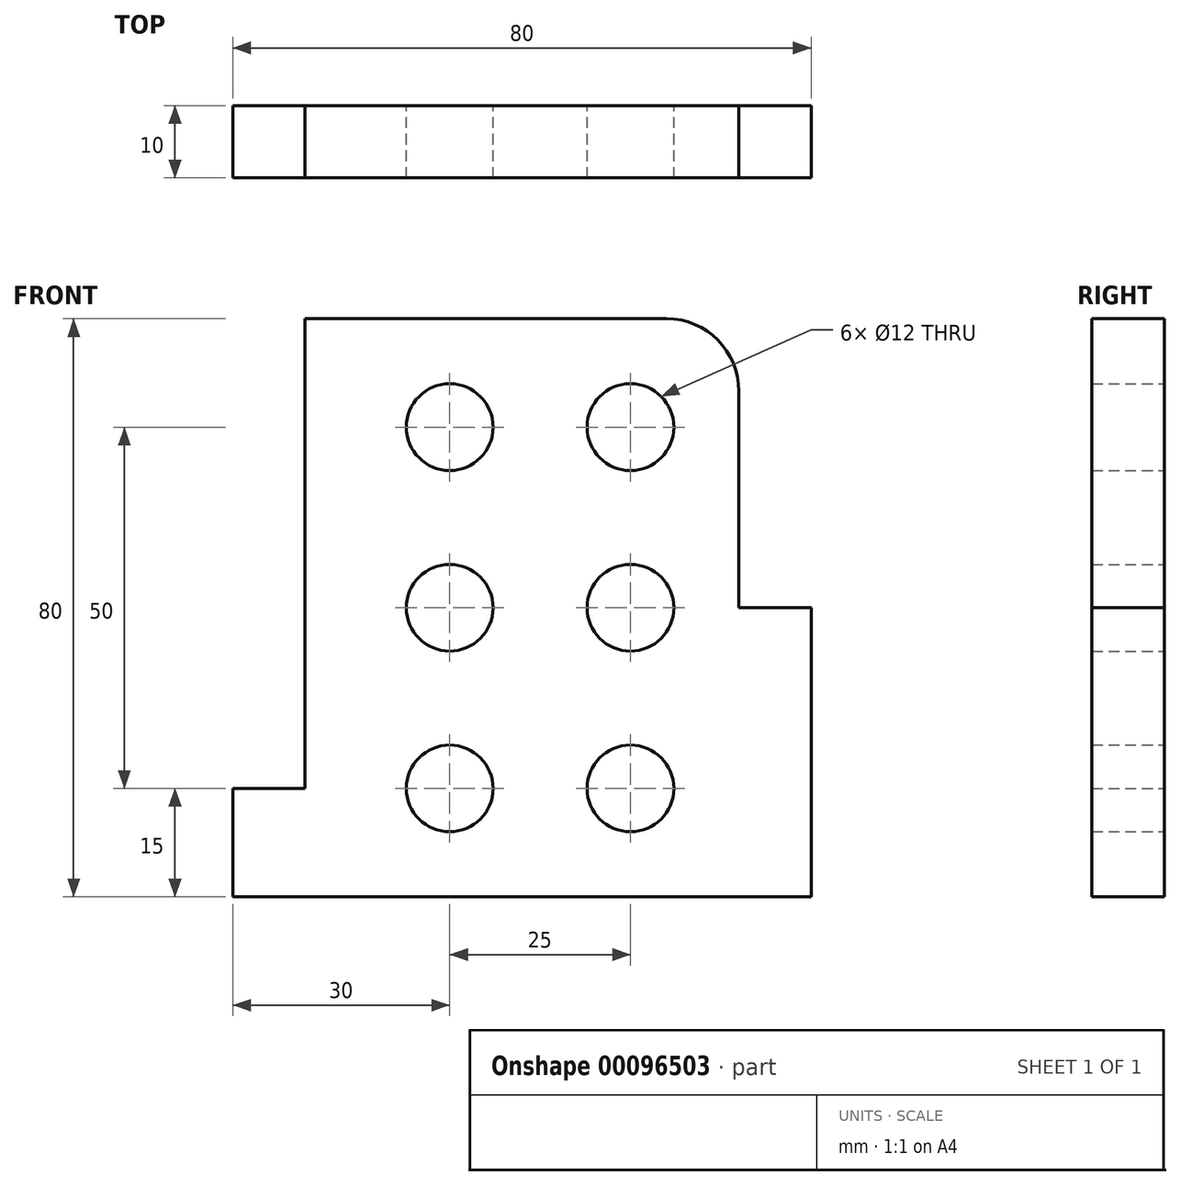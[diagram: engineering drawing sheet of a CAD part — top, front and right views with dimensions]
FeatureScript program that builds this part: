
annotation { "Feature Type Name" : "Feature", "Feature Type Description" : "" }
export const myFeature = defineFeature(function(context is Context, id is Id, definition is map)
    precondition{}
    {
        {
            var Q0;
            Q0=qCreatedBy(makeId("Front.planeOp"),FACE);
            var sketch = newSketch(context, id + "F0", { "sketchPlane" : qUnion([Q0])});
            skLineSegment(sketch, "E0", {"start": v(0, 0) * mm, "end": v(0, 15) * mm});
            skLineSegment(sketch, "E1", {"start": v(0, 15) * mm, "end": v(10, 15) * mm});
            skLineSegment(sketch, "E2", {"start": v(10, 15) * mm, "end": v(10, 80) * mm});
            skLineSegment(sketch, "E3", {"start": v(0, 0) * mm, "end": v(80, 0) * mm});
            skLineSegment(sketch, "E4", {"start": v(80, 0) * mm, "end": v(80, 40) * mm});
            skLineSegment(sketch, "E5", {"start": v(80, 40) * mm, "end": v(70, 40) * mm});
            skLineSegment(sketch, "E6", {"start": v(70, 40) * mm, "end": v(70, 70) * mm});
            skLineSegment(sketch, "E7", {"start": v(60, 80) * mm, "end": v(10, 80) * mm});
            skPoint(sketch, "E8.visualSharp", {"position": v(70, 80) * mm});
            skArc(sketch, "E8.filletArc", {"start": v(70, 70) * mm, "mid": v(67.07, 77.07) * mm, "end": v(60, 80) * mm});
            skCircle(sketch, "E9", {"center": v(30, 65) * mm, "radius": 6 * mm});
            skCircle(sketch, "E10", {"center": v(30, 40) * mm, "radius": 6 * mm});
            skCircle(sketch, "E11", {"center": v(30, 15) * mm, "radius": 6 * mm});
            skCircle(sketch, "E12", {"center": v(55, 15) * mm, "radius": 6 * mm});
            skCircle(sketch, "E13", {"center": v(55, 40) * mm, "radius": 6 * mm});
            skCircle(sketch, "E14", {"center": v(55, 65) * mm, "radius": 6 * mm});
            skSolve(sketch);
        }
        {
            var Q0;
            Q0 = qSketchRegion(id + "F0", true);
            extrude(context, id + "F1", {"entities" : qUnion([Q0]), "depth" : 10 * mm});
        }
    });
